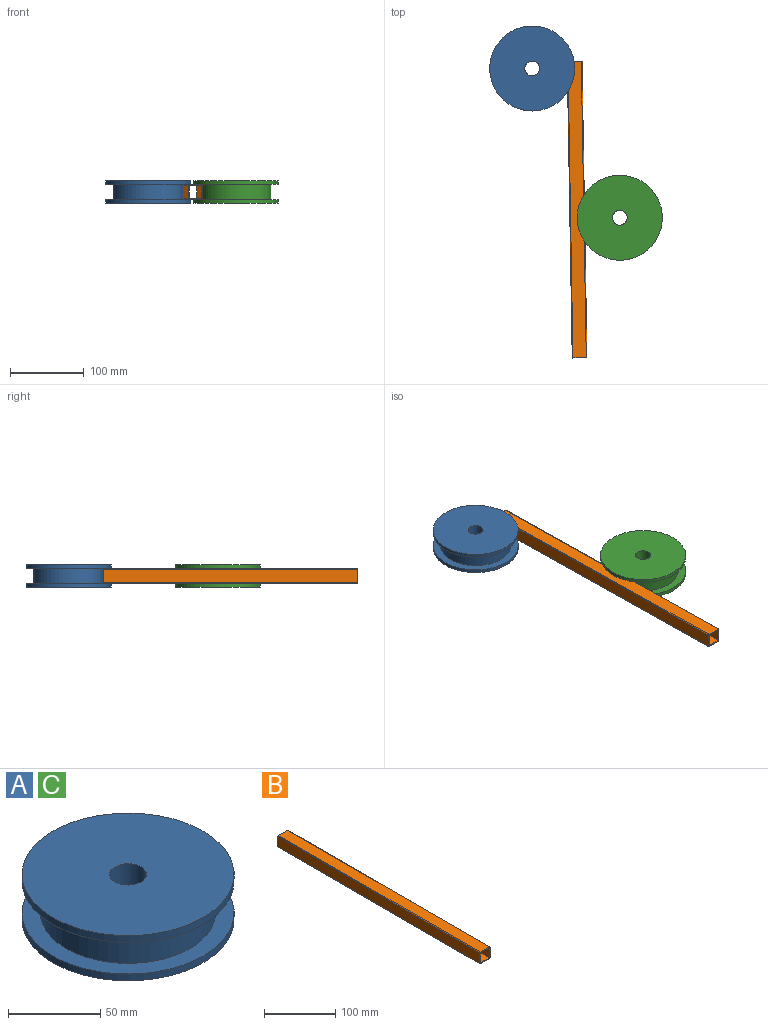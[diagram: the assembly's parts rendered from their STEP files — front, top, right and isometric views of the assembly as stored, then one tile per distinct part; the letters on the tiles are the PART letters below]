
ASSEMBLY  parts=3 mates=3
PART A: 8 faces, bbox 115x115x30 mm
  f0: cylinder r=10mm len=30mm, axis (0,0,1), area 1885mm2, adj f1,f7
  f1: plane 115x115mm, normal (0,0,1), area 10072.7mm2, adj f0,f2
  f2: cylinder r=57.5mm len=115mm, axis (0,0,1), area 1625.8mm2, adj f1,f3
  f3: plane 115x115mm, normal (0,0,-1), area 3298.7mm2, adj f2,f4
  f4: cylinder r=47.5mm len=95mm, axis (0,0,1), area 6267.5mm2, adj f3,f5
  f5: plane 115x115mm, normal (0,0,1), area 3298.7mm2, adj f4,f6
  f6: cylinder r=57.5mm len=115mm, axis (0,0,1), area 1625.8mm2, adj f5,f7
  f7: plane 115x115mm, normal (0,0,-1), area 10072.7mm2, adj f0,f6
PART B: 14 faces, bbox 20x400x20 mm
  f0: plane 400x18mm, normal (-1,0,0), area 7200mm2, adj f1,f11,f12,f13
  f1: cylinder r=1mm len=400mm, axis (0,1,0), area 628.3mm2, adj f0,f2,f12,f13
  f2: plane 400x18mm, normal (0,0,-1), area 7200mm2, adj f1,f3,f12,f13
  f3: cylinder r=1mm len=400mm, axis (0,1,0), area 628.3mm2, adj f2,f4,f12,f13
  f4: plane 400x18mm, normal (1,0,0), area 7200mm2, adj f3,f5,f12,f13
  f5: cylinder r=1mm len=400mm, axis (0,1,0), area 628.3mm2, adj f4,f6,f12,f13
  f6: plane 400x18mm, normal (0,0,1), area 7200mm2, adj f5,f11,f12,f13
  f7: plane 400x17mm, normal (0,0,-1), area 6800mm2, adj f8,f10,f12,f13
  f8: plane 400x17mm, normal (-1,0,0), area 6800mm2, adj f7,f9,f12,f13
  f9: plane 400x17mm, normal (0,0,1), area 6800mm2, adj f8,f10,f12,f13
  f10: plane 400x17mm, normal (1,0,0), area 6800mm2, adj f7,f9,f12,f13
  f11: cylinder r=1mm len=400mm, axis (0,1,0), area 628.3mm2, adj f0,f6,f12,f13
  f12: plane 20x20mm, normal (0,-1,0), area 110.1mm2, adj f0,f1,f2,f3,f4,f5,f6,f7
  f13: plane 20x20mm, normal (0,1,0), area 110.1mm2, adj f0,f1,f2,f3,f4,f5,f6,f7
PART C: same geometry as A
PLACE A rot(axis=(0,0,-1),54.3deg) t=(-118.4,201.77,15)mm
PLACE B rot(axis=(-0.01,1,0.01),90deg) t=(-58.02,10.54,-42.5)mm
PLACE C t=(0,0,15)mm
MATE parallel B.f0 <-> C.f0  axis (0,0,1) through (-57.69,10.55,25)mm
MATE planar B.f0 <-> C.f0  axis (0,0,1) through (-57.69,10.55,25)mm
MATE planar A.f0 <-> C.f0  axis (0,0,1) through (-118.4,201.77,30)mm
